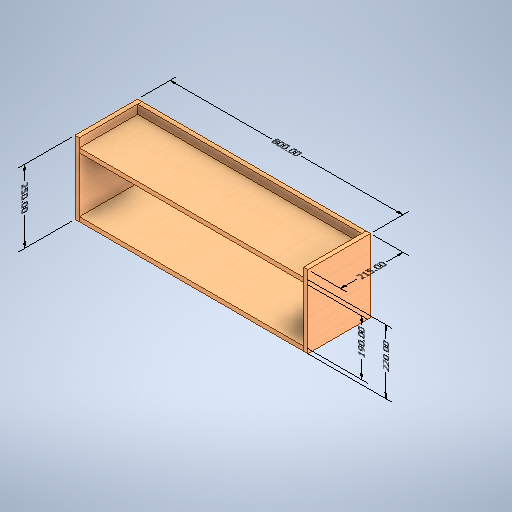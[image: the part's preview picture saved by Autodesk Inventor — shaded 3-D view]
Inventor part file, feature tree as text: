
AUTODESK INVENTOR PART (.ipt)
format: ipt  version: 2025.3 (Build 293356000, 356)  size: 360,960 bytes
history: native  units: mm
features: other x14, sketch x5, extrude x4, direct_edit x1, mirror x1, pattern_linear x1, move_body x1
ambient origin geometry x8: Origin, YZ Plane, XZ Plane, XY Plane, X Axis, Y Axis, Z Axis, Center Point
bodies: Body1 (feature_tree), Body2 (feature_tree), Body3 (feature_tree), Body4 (feature_tree), Body5 (feature_tree), Body6 (feature_tree)
feature tree (27):
  other  "ITEM1"
  other  "Annotations"
  sketch  "Sketch1"  dims[d0=800.0mm d1=250.0mm]
  sketch  "Sketch2"  dims[d2=800.0mm d3=200.0mm]
  sketch  "Sketch3"  dims[d4=15.0mm d5=200.0mm]
  extrude  "Extrusion1"  Depth=250.0mm
  direct_edit  "Direct Edit1"
  mirror  "Mirror1"
  extrude  "Extrusion2"  Depth=200.0mm
  pattern_linear  "Rectangular Pattern1"  Count1=20  [1 undecoded]
  sketch  "Sketch5"  dims[d8=200.0mm d9=0.0mm d10=20.0mm d12=205.0mm d13=0.0mm d14=0.0mm d15=15.0mm d16=90.0mm d17=90.0mm d18=15.0mm d19=0.0mm d20=15.0mm d21=0.0mm d22=250.0mm d23=3.925633mm d24=2.496534mm d25=800.0mm d26=0.0mm d27=10.0mm d28=215.0mm d29=9.556611mm d30=0.407419mm d31=190.0mm d32=0.34368mm d33=9.244926mm d34=220.0mm]
  extrude  "Extrusion3"  Depth=15.0mm
  extrude  "Extrusion4"  TaperAngle=0.0deg  [1 undecoded]
  other  "Pattern of ITEM1:1"
  other  "ITEM1A"
  sketch  "Sketch4"  dims[d6=0.0mm d7=15.0mm]
  other  "ITEM2"
  other  "Pattern of ITEM2:2"
  other  "ITEM2A"
  other  "ITEM3"
  other  "ITEM3A"
  move_body  "Move1"
  other  "Linear Dimension 1"
  other  "Linear Dimension 2"
  other  "Linear Dimension 3"
  other  "Linear Dimension 4"
  other  "Linear Dimension 5"
note: 2 required parameter values undecoded (feature->parameter linkage not recoverable at this tier; creation-order binding heuristic only, values carry confidence <= 0.55)
